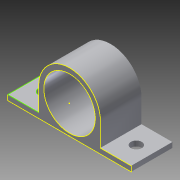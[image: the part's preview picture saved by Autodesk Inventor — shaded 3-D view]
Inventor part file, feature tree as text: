
AUTODESK INVENTOR PART (.ipt)
format: ipt  version: 2013 (Build 170138000, 138)  size: 145,408 bytes
history: native  units: in
note: dims shown in document units (in); Inventor stores cm internally (conversion verified against a paired STEP export)
features: sketch x5, extrude x2
ambient origin geometry x8: Origin, YZ Plane, XZ Plane, XY Plane, X Axis, Y Axis, Z Axis, Center Point
bodies: Solid1 (feature_tree)
feature tree (7):
  extrude  "Extrusion1"  Depth=1.5in
  extrude  "Extrusion2"  Depth=0.6875in
  sketch  "Sketch3"  dims[d4=1.25in]
  sketch  "Sketch4"  dims[d5=0.125in]
  sketch  "Sketch5"  dims[d6=1.0in d7=0.0in d8=0.266in d11=1.0in d12=0.0in d13=0.375in d14=0.266in d15=0.375in]
  sketch  "Sketch1"  dims[d0=1.5in d1=1.5in]
  sketch  "Sketch2"  dims[d2=0.125in d3=0.6875in]
